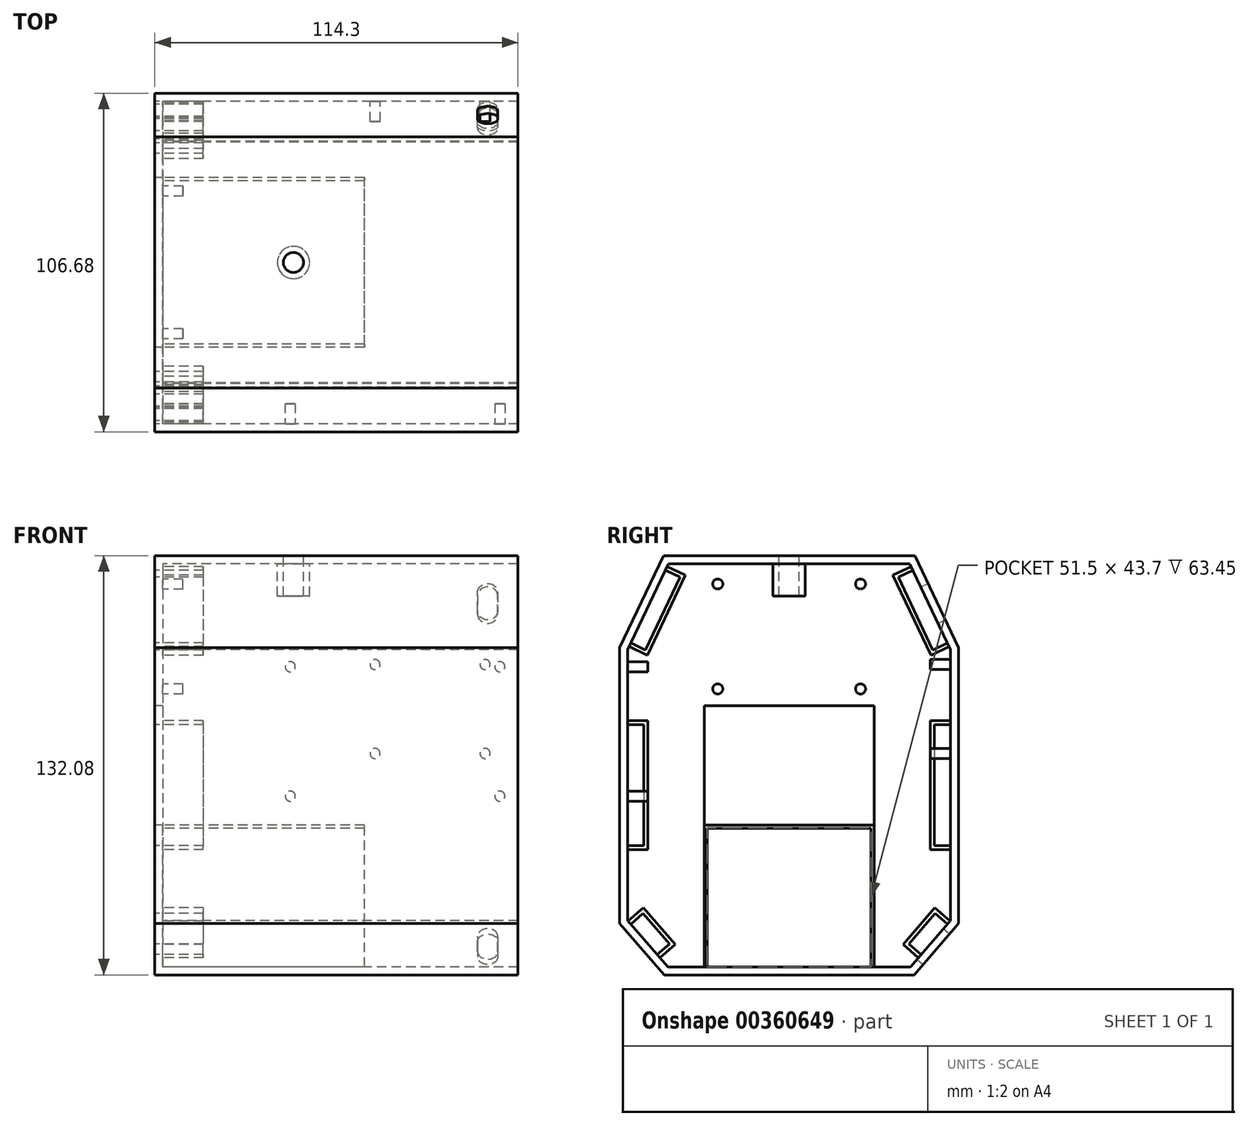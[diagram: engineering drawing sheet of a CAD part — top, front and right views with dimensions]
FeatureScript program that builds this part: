
annotation { "Feature Type Name" : "Feature", "Feature Type Description" : "" }
export const myFeature = defineFeature(function(context is Context, id is Id, definition is map)
    precondition{}
    {
        {
            var Q0;
            Q0=qCreatedBy(makeId("Right.planeOp"),FACE);
            var sketch = newSketch(context, id + "F0", { "sketchPlane" : qUnion([Q0])});
            skLineSegment(sketch, "E0", {"start": v(39.57, 53.44) * mm, "end": v(-39.57, 53.44) * mm});
            skLineSegment(sketch, "E1", {"start": v(-39.57, 53.44) * mm, "end": v(-53.34, 24.43) * mm});
            skLineSegment(sketch, "E2", {"start": v(-53.34, 24.43) * mm, "end": v(-53.34, -62.47) * mm});
            skLineSegment(sketch, "E3", {"start": v(-39.3, -78.64) * mm, "end": v(39.3, -78.64) * mm});
            skLineSegment(sketch, "E4", {"start": v(53.34, -62.47) * mm, "end": v(53.34, 24.43) * mm});
            skLineSegment(sketch, "E5", {"start": v(53.34, 24.43) * mm, "end": v(39.57, 53.44) * mm});
            skLineSegment(sketch, "E6", {"start": v(0, 53.44) * mm, "end": v(0, -78.64) * mm, "construction": true});
            skLineSegment(sketch, "E7", {"start": v(-53.34, -62.47) * mm, "end": v(-39.3, -78.64) * mm});
            skLineSegment(sketch, "E8", {"start": v(39.3, -78.64) * mm, "end": v(53.34, -62.47) * mm});
            skLineSegment(sketch, "E9.0", {"start": v(-50.8, 23.86) * mm, "end": v(-50.8, -61.52) * mm});
            skLineSegment(sketch, "E9.1", {"start": v(-37.96, 50.9) * mm, "end": v(-50.8, 23.86) * mm});
            skLineSegment(sketch, "E9.2", {"start": v(-50.8, -61.52) * mm, "end": v(-38.15, -76.1) * mm});
            skLineSegment(sketch, "E9.3", {"start": v(37.96, 50.9) * mm, "end": v(-37.96, 50.9) * mm});
            skLineSegment(sketch, "E9.4", {"start": v(-38.15, -76.1) * mm, "end": v(38.15, -76.1) * mm});
            skLineSegment(sketch, "E9.5", {"start": v(38.15, -76.1) * mm, "end": v(50.8, -61.52) * mm});
            skLineSegment(sketch, "E9.6", {"start": v(50.8, -61.52) * mm, "end": v(50.8, 23.86) * mm});
            skLineSegment(sketch, "E9.7", {"start": v(50.8, 23.86) * mm, "end": v(37.96, 50.9) * mm});
            skSolve(sketch);
        }
        {
            var Q0;
            Q0 = qSketchRegion(id + "F0", true);
            var Q1;
            Q1=makeQuery(id+"F0.imprint","IMPRINT",FACE,{"disambiguationData":[TD([[makeQuery(id+"F0.imprint","IMPRINT",EDGE,{"derivedFrom":sQuery(id+"F0.wireOp",EDGE,"E9.0")}),1.0]])]});
            extrude(context, id + "F1", {"entities" : qUnion([Q0, Q1]), "depth" : 2.54 * mm});
        }
        {
            var Q0;
            Q0 = qSketchRegion(id + "F0", true);
            extrude(context, id + "F2", {"entities" : qUnion([Q0]), "operationType" : NewBodyOperationType.ADD, "depth" : 114.3 * mm});
        }
        {
            var Q0;
            Q0=makeQuery(id+"F1.opExtrude","CAP_FACE",FACE,{"disambiguationData":[OSD([sQuery(id+"F0.wireOp",EDGE,"E0"),sQuery(id+"F0.wireOp",EDGE,"E1"),sQuery(id+"F0.wireOp",EDGE,"E2"),sQuery(id+"F0.wireOp",EDGE,"E3"),sQuery(id+"F0.wireOp",EDGE,"E4"),sQuery(id+"F0.wireOp",EDGE,"E5"),sQuery(id+"F0.wireOp",EDGE,"E7"),sQuery(id+"F0.wireOp",EDGE,"E8")])],"isStart":false});
            var sketch = newSketch(context, id + "F3", { "sketchPlane" : qUnion([Q0])});
            skLineSegment(sketch, "E10.bottom", {"start": v(-22.47, 44.49) * mm, "end": v(22.47, 44.49) * mm, "construction": true});
            skLineSegment(sketch, "E10.top", {"start": v(-22.47, 11.44) * mm, "end": v(22.47, 11.44) * mm, "construction": true});
            skLineSegment(sketch, "E10.left", {"start": v(-22.47, 44.49) * mm, "end": v(-22.47, 11.44) * mm, "construction": true});
            skLineSegment(sketch, "E10.right", {"start": v(22.47, 44.49) * mm, "end": v(22.47, 11.44) * mm, "construction": true});
            skCircle(sketch, "E11", {"center": v(-22.47, 44.49) * mm, "radius": 1.59 * mm});
            skCircle(sketch, "E12", {"center": v(22.47, 44.49) * mm, "radius": 1.59 * mm});
            skCircle(sketch, "E13", {"center": v(22.47, 11.44) * mm, "radius": 1.59 * mm});
            skCircle(sketch, "E14", {"center": v(-22.47, 11.44) * mm, "radius": 1.59 * mm});
            skSolve(sketch);
        }
        {
            var Q0;
            Q0 = qSketchRegion(id + "F3", true);
            extrude(context, id + "F4", {"entities" : qUnion([Q0]), "operationType" : NewBodyOperationType.ADD, "depth" : 6.35 * mm});
        }
        {
            var Q0;
            Q0=makeQuery(id+"F1.opExtrude","CAP_FACE",FACE,{"disambiguationData":[OSD([sQuery(id+"F0.wireOp",EDGE,"E0"),sQuery(id+"F0.wireOp",EDGE,"E1"),sQuery(id+"F0.wireOp",EDGE,"E2"),sQuery(id+"F0.wireOp",EDGE,"E3"),sQuery(id+"F0.wireOp",EDGE,"E4"),sQuery(id+"F0.wireOp",EDGE,"E5"),sQuery(id+"F0.wireOp",EDGE,"E7"),sQuery(id+"F0.wireOp",EDGE,"E8")])],"isStart":false});
            var sketch = newSketch(context, id + "F5", { "sketchPlane" : qUnion([Q0])});
            skLineSegment(sketch, "E15.bottom", {"start": v(-26.75, -76.1) * mm, "end": v(26.75, -76.1) * mm});
            skLineSegment(sketch, "E15.top", {"start": v(-26.75, -31.4) * mm, "end": v(26.75, -31.4) * mm});
            skLineSegment(sketch, "E15.left", {"start": v(-26.75, -76.1) * mm, "end": v(-26.75, -31.4) * mm});
            skLineSegment(sketch, "E15.right", {"start": v(26.75, -76.1) * mm, "end": v(26.75, -31.4) * mm});
            skLineSegment(sketch, "E16.bottom", {"start": v(-25.75, -76.1) * mm, "end": v(25.75, -76.1) * mm});
            skLineSegment(sketch, "E16.top", {"start": v(-25.75, -32.4) * mm, "end": v(25.75, -32.4) * mm});
            skLineSegment(sketch, "E16.left", {"start": v(-25.75, -76.1) * mm, "end": v(-25.75, -32.4) * mm});
            skLineSegment(sketch, "E16.right", {"start": v(25.75, -76.1) * mm, "end": v(25.75, -32.4) * mm});
            skPoint(sketch, "E17", {"position": v(0, -31.4) * mm});
            skPoint(sketch, "E18", {"position": v(0, -32.4) * mm});
            skSolve(sketch);
        }
        {
            var Q0;
            Q0=makeQuery(id+"F5.imprint","IMPRINT",FACE,{"disambiguationData":[TD([[makeQuery(id+"F5.imprint","IMPRINT",EDGE,{"derivedFrom":sQuery(id+"F5.wireOp",EDGE,"E15.top")}),-1.0]])]});
            extrude(context, id + "F6", {"entities" : qUnion([Q0]), "operationType" : NewBodyOperationType.ADD, "depth" : 63.45 * mm});
        }
        {
            var Q0;
            Q0=makeQuery(id+"F2.opExtrude","SWEPT_FACE",FACE,{"disambiguationData":[OSD([sQuery(id+"F0.wireOp",EDGE,"E9.0")])]});
            var sketch = newSketch(context, id + "F7", { "sketchPlane" : qUnion([Q0])});
            skLineSegment(sketch, "E19.bottom", {"start": v(-108.58, 18.43) * mm, "end": v(-42.64, 18.43) * mm, "construction": true});
            skLineSegment(sketch, "E19.top", {"start": v(-108.58, -22.34) * mm, "end": v(-42.64, -22.34) * mm, "construction": true});
            skLineSegment(sketch, "E19.left", {"start": v(-108.58, 18.43) * mm, "end": v(-108.58, -22.34) * mm, "construction": true});
            skLineSegment(sketch, "E19.right", {"start": v(-42.64, 18.43) * mm, "end": v(-42.64, -22.34) * mm, "construction": true});
            skCircle(sketch, "E20", {"center": v(-108.58, 18.43) * mm, "radius": 1.59 * mm});
            skCircle(sketch, "E21", {"center": v(-108.58, -22.34) * mm, "radius": 1.59 * mm});
            skCircle(sketch, "E22", {"center": v(-42.64, -22.34) * mm, "radius": 1.59 * mm});
            skCircle(sketch, "E23", {"center": v(-42.64, 18.43) * mm, "radius": 1.59 * mm});
            skSolve(sketch);
        }
        {
            var Q0;
            Q0 = qSketchRegion(id + "F7", true);
            extrude(context, id + "F8", {"entities" : qUnion([Q0]), "operationType" : NewBodyOperationType.ADD, "depth" : 6.35 * mm});
        }
        {
            var Q0;
            Q0=makeQuery(id+"F2.opExtrude","SWEPT_FACE",FACE,{"disambiguationData":[OSD([sQuery(id+"F0.wireOp",EDGE,"E9.6")])]});
            var sketch = newSketch(context, id + "F9", { "sketchPlane" : qUnion([Q0])});
            skLineSegment(sketch, "E24.bottom", {"start": v(69.32, 19.12) * mm, "end": v(103.97, 19.12) * mm, "construction": true});
            skLineSegment(sketch, "E24.top", {"start": v(69.32, -8.9) * mm, "end": v(103.97, -8.9) * mm, "construction": true});
            skLineSegment(sketch, "E24.left", {"start": v(69.32, 19.12) * mm, "end": v(69.32, -8.9) * mm, "construction": true});
            skLineSegment(sketch, "E24.right", {"start": v(103.97, 19.12) * mm, "end": v(103.97, -8.9) * mm, "construction": true});
            skCircle(sketch, "E25", {"center": v(103.97, 19.12) * mm, "radius": 1.59 * mm});
            skCircle(sketch, "E26", {"center": v(69.32, 19.12) * mm, "radius": 1.59 * mm});
            skCircle(sketch, "E27", {"center": v(69.32, -8.9) * mm, "radius": 1.59 * mm});
            skCircle(sketch, "E28", {"center": v(103.97, -8.9) * mm, "radius": 1.59 * mm});
            skSolve(sketch);
        }
        {
            var Q0;
            Q0 = qSketchRegion(id + "F9", true);
            extrude(context, id + "F10", {"entities" : qUnion([Q0]), "operationType" : NewBodyOperationType.ADD, "depth" : 6.35 * mm});
        }
        {
            var Q0;
            Q0=makeQuery(id+"F6.boolean.opBoolean","SPLIT",FACE,{"disambiguationData":[TD([makeQuery(id+"F2.opExtrude","SWEPT_FACE",FACE,{"disambiguationData":[OSD([sQuery(id+"F0.wireOp",EDGE,"E9.0")])]})])],"derivedFrom":makeQuery(id+"F1.opExtrude","CAP_FACE",FACE,{"disambiguationData":[OSD([sQuery(id+"F0.wireOp",EDGE,"E0"),sQuery(id+"F0.wireOp",EDGE,"E1"),sQuery(id+"F0.wireOp",EDGE,"E2"),sQuery(id+"F0.wireOp",EDGE,"E3"),sQuery(id+"F0.wireOp",EDGE,"E4"),sQuery(id+"F0.wireOp",EDGE,"E5"),sQuery(id+"F0.wireOp",EDGE,"E7"),sQuery(id+"F0.wireOp",EDGE,"E8")])],"isStart":false})});
            var sketch = newSketch(context, id + "F11", { "sketchPlane" : qUnion([Q0])});
            skPoint(sketch, "E29", {"position": v(-44.38, 37.38) * mm});
            skPoint(sketch, "E30", {"position": v(-50.8, -18.83) * mm});
            skPoint(sketch, "E31", {"position": v(-45.67, -67.44) * mm});
            skLineSegment(sketch, "E32", {"start": v(-46, -59.31) * mm, "end": v(-37.67, -68.9) * mm});
            skLineSegment(sketch, "E33", {"start": v(-50.8, 0.22) * mm, "end": v(-45.72, 0.22) * mm});
            skLineSegment(sketch, "E34", {"start": v(-45.72, 0.22) * mm, "end": v(-45.72, -37.88) * mm});
            skLineSegment(sketch, "E35", {"start": v(-45.72, -37.88) * mm, "end": v(-50.8, -37.88) * mm});
            skLineSegment(sketch, "E36", {"start": v(-38.94, 48.85) * mm, "end": v(-34.35, 46.67) * mm});
            skLineSegment(sketch, "E37", {"start": v(-34.35, 46.67) * mm, "end": v(-45.24, 23.73) * mm});
            skLineSegment(sketch, "E38", {"start": v(-45.24, 23.73) * mm, "end": v(-49.83, 25.9) * mm});
            skLineSegment(sketch, "E39", {"start": v(-49.83, -62.64) * mm, "end": v(-46, -59.31) * mm});
            skLineSegment(sketch, "E40", {"start": v(-41.5, -72.23) * mm, "end": v(-37.67, -68.9) * mm});
            skLineSegment(sketch, "E41.0", {"start": v(-32.66, 47.28) * mm, "end": v(-44.64, 22.04) * mm});
            skLineSegment(sketch, "E41.1", {"start": v(-38.4, 50) * mm, "end": v(-32.66, 47.28) * mm});
            skLineSegment(sketch, "E41.3", {"start": v(-44.64, 22.04) * mm, "end": v(-50.37, 24.76) * mm});
            skLineSegment(sketch, "E42.0", {"start": v(-44.45, -39.15) * mm, "end": v(-50.8, -39.15) * mm});
            skLineSegment(sketch, "E42.1", {"start": v(-44.45, 1.49) * mm, "end": v(-44.45, -39.15) * mm});
            skLineSegment(sketch, "E42.2", {"start": v(-50.8, 1.49) * mm, "end": v(-44.45, 1.49) * mm});
            skLineSegment(sketch, "E43.0", {"start": v(-45.86, -57.52) * mm, "end": v(-35.88, -69.03) * mm});
            skLineSegment(sketch, "E43.1", {"start": v(-50.66, -61.68) * mm, "end": v(-45.86, -57.52) * mm});
            skLineSegment(sketch, "E43.3", {"start": v(-40.67, -73.2) * mm, "end": v(-35.88, -69.03) * mm});
            skLineSegment(sketch, "E44", {"start": v(-50.8, -61.52) * mm, "end": v(-49.83, -62.64) * mm});
            skLineSegment(sketch, "E45", {"start": v(-50.8, -39.15) * mm, "end": v(-50.8, -37.88) * mm});
            skLineSegment(sketch, "E46", {"start": v(-50.37, 24.76) * mm, "end": v(-49.83, 25.9) * mm});
            skLineSegment(sketch, "E47", {"start": v(0, 50.9) * mm, "end": v(0, -78.26) * mm, "construction": true});
            skLineSegment(sketch, "E48.MirrorCS", {"start": v(44.45, -39.15) * mm, "end": v(50.8, -39.15) * mm});
            skLineSegment(sketch, "E49.MirrorCS", {"start": v(45.72, -37.88) * mm, "end": v(50.8, -37.88) * mm});
            skLineSegment(sketch, "E50.MirrorCS", {"start": v(50.8, 1.49) * mm, "end": v(44.45, 1.49) * mm});
            skLineSegment(sketch, "E51.MirrorCS", {"start": v(41.5, -72.23) * mm, "end": v(37.67, -68.9) * mm});
            skLineSegment(sketch, "E52.MirrorCS", {"start": v(45.24, 23.73) * mm, "end": v(49.83, 25.9) * mm});
            skLineSegment(sketch, "E53.MirrorCS", {"start": v(50.8, 0.22) * mm, "end": v(45.72, 0.22) * mm});
            skLineSegment(sketch, "E54.MirrorCS", {"start": v(40.67, -73.2) * mm, "end": v(35.88, -69.03) * mm});
            skLineSegment(sketch, "E55.MirrorCS", {"start": v(49.83, -62.64) * mm, "end": v(46, -59.31) * mm});
            skLineSegment(sketch, "E56.MirrorCS", {"start": v(50.66, -61.68) * mm, "end": v(45.86, -57.52) * mm});
            skLineSegment(sketch, "E57.MirrorCS", {"start": v(50.8, -61.52) * mm, "end": v(49.83, -62.64) * mm});
            skLineSegment(sketch, "E58.MirrorCS", {"start": v(38.94, 48.85) * mm, "end": v(34.35, 46.67) * mm});
            skLineSegment(sketch, "E59.MirrorCS", {"start": v(46, -59.31) * mm, "end": v(37.67, -68.9) * mm});
            skLineSegment(sketch, "E60.MirrorCS", {"start": v(44.64, 22.04) * mm, "end": v(50.37, 24.76) * mm});
            skLineSegment(sketch, "E61.MirrorCS", {"start": v(38.4, 50) * mm, "end": v(32.66, 47.28) * mm});
            skLineSegment(sketch, "E62.MirrorCS", {"start": v(50.37, 24.76) * mm, "end": v(49.83, 25.9) * mm});
            skLineSegment(sketch, "E63.MirrorCS", {"start": v(32.66, 47.28) * mm, "end": v(44.64, 22.04) * mm});
            skLineSegment(sketch, "E64.MirrorCS", {"start": v(45.86, -57.52) * mm, "end": v(35.88, -69.03) * mm});
            skLineSegment(sketch, "E65.MirrorCS", {"start": v(34.35, 46.67) * mm, "end": v(45.24, 23.73) * mm});
            skLineSegment(sketch, "E66.MirrorCS", {"start": v(44.45, 1.49) * mm, "end": v(44.45, -39.15) * mm});
            skLineSegment(sketch, "E67.MirrorCS", {"start": v(50.8, -39.15) * mm, "end": v(50.8, -37.88) * mm});
            skPoint(sketch, "E68.MirrorP", {"position": v(50.8, -18.83) * mm});
            skLineSegment(sketch, "E69.MirrorCS", {"start": v(45.72, 0.22) * mm, "end": v(45.72, -37.88) * mm});
            skPoint(sketch, "E70.MirrorP", {"position": v(45.67, -67.44) * mm});
            skPoint(sketch, "E71.MirrorP", {"position": v(44.38, 37.38) * mm});
            skLineSegment(sketch, "E72.trimOffspring", {"start": v(-50.8, 0.22) * mm, "end": v(-50.8, 1.49) * mm});
            skLineSegment(sketch, "E73.trimOffspring", {"start": v(41.5, -72.23) * mm, "end": v(40.67, -73.2) * mm});
            skLineSegment(sketch, "E74.trimOffspring", {"start": v(50.8, 0.22) * mm, "end": v(50.8, 1.49) * mm});
            skLineSegment(sketch, "E75.trimOffspring", {"start": v(-38.94, 48.85) * mm, "end": v(-38.4, 50) * mm});
            skLineSegment(sketch, "E76.trimOffspring", {"start": v(38.94, 48.85) * mm, "end": v(38.4, 50) * mm});
            skLineSegment(sketch, "E77", {"start": v(49.83, 25.9) * mm, "end": v(50.37, 24.76) * mm});
            skLineSegment(sketch, "E78", {"start": v(50.66, -61.68) * mm, "end": v(49.83, -62.64) * mm});
            skLineSegment(sketch, "E79", {"start": v(-40.67, -73.2) * mm, "end": v(-41.5, -72.23) * mm});
            skLineSegment(sketch, "E80", {"start": v(-49.83, -62.64) * mm, "end": v(-50.66, -61.68) * mm});
            skSolve(sketch);
        }
        {
            var Q0;
            Q0 = qSketchRegion(id + "F11", true);
            extrude(context, id + "F12", {"entities" : qUnion([Q0]), "operationType" : NewBodyOperationType.ADD, "depth" : 12.7 * mm});
        }
        {
            var Q0;
            Q0=makeQuery(id+"F12.boolean.opBoolean","SPLIT",FACE,{"disambiguationData":[TD([makeQuery(id+"F12.opExtrude","SWEPT_FACE",FACE,{"disambiguationData":[OSD([sQuery(id+"F11.wireOp",EDGE,"E36")])]})])],"derivedFrom":makeQuery(id+"F6.boolean.opBoolean","SPLIT",FACE,{"disambiguationData":[TD([makeQuery(id+"F2.opExtrude","SWEPT_FACE",FACE,{"disambiguationData":[OSD([sQuery(id+"F0.wireOp",EDGE,"E9.0")])]})])],"derivedFrom":makeQuery(id+"F1.opExtrude","CAP_FACE",FACE,{"disambiguationData":[OSD([sQuery(id+"F0.wireOp",EDGE,"E0"),sQuery(id+"F0.wireOp",EDGE,"E1"),sQuery(id+"F0.wireOp",EDGE,"E2"),sQuery(id+"F0.wireOp",EDGE,"E3"),sQuery(id+"F0.wireOp",EDGE,"E4"),sQuery(id+"F0.wireOp",EDGE,"E5"),sQuery(id+"F0.wireOp",EDGE,"E7"),sQuery(id+"F0.wireOp",EDGE,"E8")])],"isStart":false})})});
            var Q1;
            {var subQ0=makeQuery(id+"F2.opExtrude","SWEPT_FACE",FACE,{"disambiguationData":[OSD([sQuery(id+"F0.wireOp",EDGE,"E9.0")])]});Q1=makeQuery(id+"F12.boolean.opBoolean","SPLIT",FACE,{"disambiguationData":[TD([makeQuery(id+"F12.opExtrude","SWEPT_FACE",FACE,{"disambiguationData":[OSD([sQuery(id+"F11.wireOp",EDGE,"E33")])]})])],"derivedFrom":makeQuery(id+"F6.boolean.opBoolean","SPLIT",FACE,{"disambiguationData":[TD([subQ0])],"derivedFrom":makeQuery(id+"F1.opExtrude","CAP_FACE",FACE,{"disambiguationData":[OSD([sQuery(id+"F0.wireOp",EDGE,"E0"),sQuery(id+"F0.wireOp",EDGE,"E1"),sQuery(id+"F0.wireOp",EDGE,"E2"),sQuery(id+"F0.wireOp",EDGE,"E3"),sQuery(id+"F0.wireOp",EDGE,"E4"),sQuery(id+"F0.wireOp",EDGE,"E5"),sQuery(id+"F0.wireOp",EDGE,"E7"),sQuery(id+"F0.wireOp",EDGE,"E8")])],"isStart":false})})});}
            var Q2;
            Q2=makeQuery(id+"F12.boolean.opBoolean","SPLIT",FACE,{"disambiguationData":[TD([makeQuery(id+"F12.opExtrude","SWEPT_FACE",FACE,{"disambiguationData":[OSD([sQuery(id+"F11.wireOp",EDGE,"E49.MirrorCS")])]})])],"derivedFrom":makeQuery(id+"F6.boolean.opBoolean","SPLIT",FACE,{"disambiguationData":[TD([makeQuery(id+"F2.opExtrude","SWEPT_FACE",FACE,{"disambiguationData":[OSD([sQuery(id+"F0.wireOp",EDGE,"E9.0")])]})])],"derivedFrom":makeQuery(id+"F1.opExtrude","CAP_FACE",FACE,{"disambiguationData":[OSD([sQuery(id+"F0.wireOp",EDGE,"E0"),sQuery(id+"F0.wireOp",EDGE,"E1"),sQuery(id+"F0.wireOp",EDGE,"E2"),sQuery(id+"F0.wireOp",EDGE,"E3"),sQuery(id+"F0.wireOp",EDGE,"E4"),sQuery(id+"F0.wireOp",EDGE,"E5"),sQuery(id+"F0.wireOp",EDGE,"E7"),sQuery(id+"F0.wireOp",EDGE,"E8")])],"isStart":false})})});
            var Q3;
            Q3=makeQuery(id+"F12.boolean.opBoolean","SPLIT",FACE,{"disambiguationData":[TD([makeQuery(id+"F12.opExtrude","SWEPT_FACE",FACE,{"disambiguationData":[OSD([sQuery(id+"F11.wireOp",EDGE,"E52.MirrorCS")])]})])],"derivedFrom":makeQuery(id+"F6.boolean.opBoolean","SPLIT",FACE,{"disambiguationData":[TD([makeQuery(id+"F2.opExtrude","SWEPT_FACE",FACE,{"disambiguationData":[OSD([sQuery(id+"F0.wireOp",EDGE,"E9.0")])]})])],"derivedFrom":makeQuery(id+"F1.opExtrude","CAP_FACE",FACE,{"disambiguationData":[OSD([sQuery(id+"F0.wireOp",EDGE,"E0"),sQuery(id+"F0.wireOp",EDGE,"E1"),sQuery(id+"F0.wireOp",EDGE,"E2"),sQuery(id+"F0.wireOp",EDGE,"E3"),sQuery(id+"F0.wireOp",EDGE,"E4"),sQuery(id+"F0.wireOp",EDGE,"E5"),sQuery(id+"F0.wireOp",EDGE,"E7"),sQuery(id+"F0.wireOp",EDGE,"E8")])],"isStart":false})})});
            var Q4;
            Q4=makeQuery(id+"F12.boolean.opBoolean","SPLIT",FACE,{"disambiguationData":[TD([makeQuery(id+"F12.opExtrude","SWEPT_FACE",FACE,{"disambiguationData":[OSD([sQuery(id+"F11.wireOp",EDGE,"E51.MirrorCS")])]})])],"derivedFrom":makeQuery(id+"F6.boolean.opBoolean","SPLIT",FACE,{"disambiguationData":[TD([makeQuery(id+"F2.opExtrude","SWEPT_FACE",FACE,{"disambiguationData":[OSD([sQuery(id+"F0.wireOp",EDGE,"E9.0")])]})])],"derivedFrom":makeQuery(id+"F1.opExtrude","CAP_FACE",FACE,{"disambiguationData":[OSD([sQuery(id+"F0.wireOp",EDGE,"E0"),sQuery(id+"F0.wireOp",EDGE,"E1"),sQuery(id+"F0.wireOp",EDGE,"E2"),sQuery(id+"F0.wireOp",EDGE,"E3"),sQuery(id+"F0.wireOp",EDGE,"E4"),sQuery(id+"F0.wireOp",EDGE,"E5"),sQuery(id+"F0.wireOp",EDGE,"E7"),sQuery(id+"F0.wireOp",EDGE,"E8")])],"isStart":false})})});
            var Q5;
            Q5=makeQuery(id+"F12.boolean.opBoolean","SPLIT",FACE,{"disambiguationData":[TD([makeQuery(id+"F12.opExtrude","SWEPT_FACE",FACE,{"disambiguationData":[OSD([sQuery(id+"F11.wireOp",EDGE,"E32")])]})])],"derivedFrom":makeQuery(id+"F6.boolean.opBoolean","SPLIT",FACE,{"disambiguationData":[TD([makeQuery(id+"F2.opExtrude","SWEPT_FACE",FACE,{"disambiguationData":[OSD([sQuery(id+"F0.wireOp",EDGE,"E9.0")])]})])],"derivedFrom":makeQuery(id+"F1.opExtrude","CAP_FACE",FACE,{"disambiguationData":[OSD([sQuery(id+"F0.wireOp",EDGE,"E0"),sQuery(id+"F0.wireOp",EDGE,"E1"),sQuery(id+"F0.wireOp",EDGE,"E2"),sQuery(id+"F0.wireOp",EDGE,"E3"),sQuery(id+"F0.wireOp",EDGE,"E4"),sQuery(id+"F0.wireOp",EDGE,"E5"),sQuery(id+"F0.wireOp",EDGE,"E7"),sQuery(id+"F0.wireOp",EDGE,"E8")])],"isStart":false})})});
            extrude(context, id + "F13", {"entities" : qUnion([Q0, Q1, Q2, Q3, Q4, Q5]), "operationType" : NewBodyOperationType.REMOVE, "oppositeDirection" : true, "depth" : 25.4 * mm});
        }
        {
            var Q0;
            {var subQ0=sQuery(id+"F0.wireOp",EDGE,"E5");Q0=makeQuery(id+"F2.boolean.opBoolean","MERGE",FACE,{"derivedFrom":[makeQuery(id+"F1.opExtrude","SWEPT_FACE",FACE,{"disambiguationData":[OSD([subQ0])]}),makeQuery(id+"F2.opExtrude","SWEPT_FACE",FACE,{"disambiguationData":[OSD([subQ0])]})]});}
            var sketch = newSketch(context, id + "F14", { "sketchPlane" : qUnion([Q0])});
            skLineSegment(sketch, "E81", {"start": v(-104.78, 31.31) * mm, "end": v(-104.78, -0.8) * mm, "construction": true});
            skArc(sketch, "E82", {"start": v(-101.6, 18.43) * mm, "mid": v(-104.78, 21.6) * mm, "end": v(-107.95, 18.43) * mm});
            skArc(sketch, "E83", {"start": v(-107.95, 12.08) * mm, "mid": v(-104.78, 8.9) * mm, "end": v(-101.6, 12.08) * mm});
            skLineSegment(sketch, "E84", {"start": v(-107.95, 18.43) * mm, "end": v(-107.95, 12.08) * mm});
            skLineSegment(sketch, "E85", {"start": v(-101.6, 12.08) * mm, "end": v(-101.6, 18.43) * mm});
            skPoint(sketch, "E86", {"position": v(-104.78, 15.26) * mm});
            skPoint(sketch, "E87", {"position": v(-104.78, 21.6) * mm});
            skPoint(sketch, "E88", {"position": v(-104.78, 8.9) * mm});
            skSolve(sketch);
        }
        {
            var Q0;
            Q0 = qSketchRegion(id + "F14", true);
            extrude(context, id + "F15", {"entities" : qUnion([Q0]), "operationType" : NewBodyOperationType.REMOVE, "oppositeDirection" : true, "depth" : 25.4 * mm});
        }
        {
            var Q0;
            {var subQ0=sQuery(id+"F0.wireOp",EDGE,"E8");Q0=makeQuery(id+"F2.boolean.opBoolean","MERGE",FACE,{"derivedFrom":[makeQuery(id+"F1.opExtrude","SWEPT_FACE",FACE,{"disambiguationData":[OSD([subQ0])]}),makeQuery(id+"F2.opExtrude","SWEPT_FACE",FACE,{"disambiguationData":[OSD([subQ0])]})]});}
            var sketch = newSketch(context, id + "F16", { "sketchPlane" : qUnion([Q0])});
            skLineSegment(sketch, "E89", {"start": v(-104.78, -12.23) * mm, "end": v(-104.78, -33.64) * mm, "construction": true});
            skArc(sketch, "E90", {"start": v(-101.6, -19.76) * mm, "mid": v(-104.78, -16.58) * mm, "end": v(-107.95, -19.76) * mm});
            skArc(sketch, "E91", {"start": v(-107.95, -26.1) * mm, "mid": v(-104.78, -29.28) * mm, "end": v(-101.6, -26.1) * mm});
            skLineSegment(sketch, "E92", {"start": v(-107.95, -19.76) * mm, "end": v(-107.95, -26.1) * mm});
            skLineSegment(sketch, "E93", {"start": v(-101.6, -19.76) * mm, "end": v(-101.6, -26.1) * mm});
            skPoint(sketch, "E94", {"position": v(-104.78, -22.93) * mm});
            skPoint(sketch, "E95", {"position": v(-104.78, -16.58) * mm});
            skPoint(sketch, "E96", {"position": v(-104.78, -29.28) * mm});
            skSolve(sketch);
        }
        {
            var Q0;
            Q0 = qSketchRegion(id + "F16", true);
            extrude(context, id + "F17", {"entities" : qUnion([Q0]), "operationType" : NewBodyOperationType.REMOVE, "oppositeDirection" : true, "depth" : 25.4 * mm});
        }
        {
            var Q0;
            Q0=makeQuery(id+"F1.opExtrude","CAP_FACE",FACE,{"disambiguationData":[OSD([sQuery(id+"F0.wireOp",EDGE,"E0"),sQuery(id+"F0.wireOp",EDGE,"E1"),sQuery(id+"F0.wireOp",EDGE,"E2"),sQuery(id+"F0.wireOp",EDGE,"E3"),sQuery(id+"F0.wireOp",EDGE,"E4"),sQuery(id+"F0.wireOp",EDGE,"E5"),sQuery(id+"F0.wireOp",EDGE,"E7"),sQuery(id+"F0.wireOp",EDGE,"E8")])],"isStart":true});
            var sketch = newSketch(context, id + "F18", { "sketchPlane" : qUnion([Q0])});
            skLineSegment(sketch, "E97.bottom", {"start": v(-26.75, 6.17) * mm, "end": v(26.75, 6.17) * mm});
            skLineSegment(sketch, "E97.left", {"start": v(-26.75, 6.17) * mm, "end": v(-26.75, -31.4) * mm});
            skLineSegment(sketch, "E97.right", {"start": v(26.75, 6.17) * mm, "end": v(26.75, -31.4) * mm});
            skPoint(sketch, "E98", {"position": v(0, 6.17) * mm});
            skLineSegment(sketch, "E99", {"start": v(26.75, -31.4) * mm, "end": v(-26.75, -31.4) * mm});
            skSolve(sketch);
        }
        {
            var Q0;
            Q0 = qSketchRegion(id + "F18", true);
            extrude(context, id + "F19", {"entities" : qUnion([Q0]), "operationType" : NewBodyOperationType.REMOVE, "oppositeDirection" : true, "depth" : 2.54 * mm});
        }
        {
            var Q0;
            Q0=makeQuery(id+"F2.opExtrude","CAP_FACE",FACE,{"disambiguationData":[OSD([sQuery(id+"F0.wireOp",EDGE,"E0"),sQuery(id+"F0.wireOp",EDGE,"E1"),sQuery(id+"F0.wireOp",EDGE,"E2"),sQuery(id+"F0.wireOp",EDGE,"E3"),sQuery(id+"F0.wireOp",EDGE,"E4"),sQuery(id+"F0.wireOp",EDGE,"E5"),sQuery(id+"F0.wireOp",EDGE,"E7"),sQuery(id+"F0.wireOp",EDGE,"E8"),sQuery(id+"F0.wireOp",EDGE,"E9.0"),sQuery(id+"F0.wireOp",EDGE,"E9.1"),sQuery(id+"F0.wireOp",EDGE,"E9.2"),sQuery(id+"F0.wireOp",EDGE,"E9.3"),sQuery(id+"F0.wireOp",EDGE,"E9.4"),sQuery(id+"F0.wireOp",EDGE,"E9.5"),sQuery(id+"F0.wireOp",EDGE,"E9.6"),sQuery(id+"F0.wireOp",EDGE,"E9.7")])],"isStart":false});
            var sketch = newSketch(context, id + "F20", { "sketchPlane" : qUnion([Q0])});
            skLineSegment(sketch, "E100.bottom", {"start": v(-71.37, -13.27) * mm, "end": v(74.2, -13.27) * mm});
            skLineSegment(sketch, "E100.top", {"start": v(-71.37, -89.6) * mm, "end": v(74.2, -89.6) * mm});
            skLineSegment(sketch, "E100.left", {"start": v(-71.37, -13.27) * mm, "end": v(-71.37, -89.6) * mm});
            skLineSegment(sketch, "E100.right", {"start": v(74.2, -13.27) * mm, "end": v(74.2, -89.6) * mm});
            skLineSegment(sketch, "E101.top", {"start": v(-71.37, 62.68) * mm, "end": v(74.2, 62.68) * mm});
            skLineSegment(sketch, "E101.left", {"start": v(-71.37, -13.27) * mm, "end": v(-71.37, 62.68) * mm});
            skLineSegment(sketch, "E101.right", {"start": v(74.2, -13.27) * mm, "end": v(74.2, 62.68) * mm});
            skSolve(sketch);
        }
        {
            var Q0;
            {var subQ0=sQuery(id+"F0.wireOp",EDGE,"E0");Q0=makeQuery(id+"F2.boolean.opBoolean","MERGE",FACE,{"derivedFrom":[makeQuery(id+"F1.opExtrude","SWEPT_FACE",FACE,{"disambiguationData":[OSD([subQ0])]}),makeQuery(id+"F2.opExtrude","SWEPT_FACE",FACE,{"disambiguationData":[OSD([subQ0])]})]});}
            var sketch = newSketch(context, id + "F21", { "sketchPlane" : qUnion([Q0])});
            skLineSegment(sketch, "E102", {"start": v(0, 0) * mm, "end": v(114.3, 0) * mm, "construction": true});
            skCircle(sketch, "E103", {"center": v(43.63, 0) * mm, "radius": 5.08 * mm});
            skCircle(sketch, "E104", {"center": v(43.63, 0) * mm, "radius": 3.18 * mm});
            skSolve(sketch);
        }
        {
            var Q0;
            Q0 = qSketchRegion(id + "F21", true);
            extrude(context, id + "F22", {"entities" : qUnion([Q0]), "operationType" : NewBodyOperationType.ADD, "oppositeDirection" : true, "depth" : 12.7 * mm});
        }
        {
            var Q0;
            Q0=makeQuery(id+"F21.imprint","IMPRINT",FACE,{"disambiguationData":[TD([[makeQuery(id+"F21.imprint","IMPRINT",EDGE,{"derivedFrom":sQuery(id+"F21.wireOp",EDGE,"E103")}),-1.0]])]});
            var sketch = newSketch(context, id + "F23", { "sketchPlane" : qUnion([Q0])});
            skCircle(sketch, "E105", {"center": v(43.63, 0) * mm, "radius": 3.18 * mm});
            skSolve(sketch);
        }
        {
            var Q0;
            Q0 = qSketchRegion(id + "F23", true);
            extrude(context, id + "F24", {"entities" : qUnion([Q0]), "operationType" : NewBodyOperationType.REMOVE, "oppositeDirection" : true, "depth" : 25.4 * mm});
        }
    });
